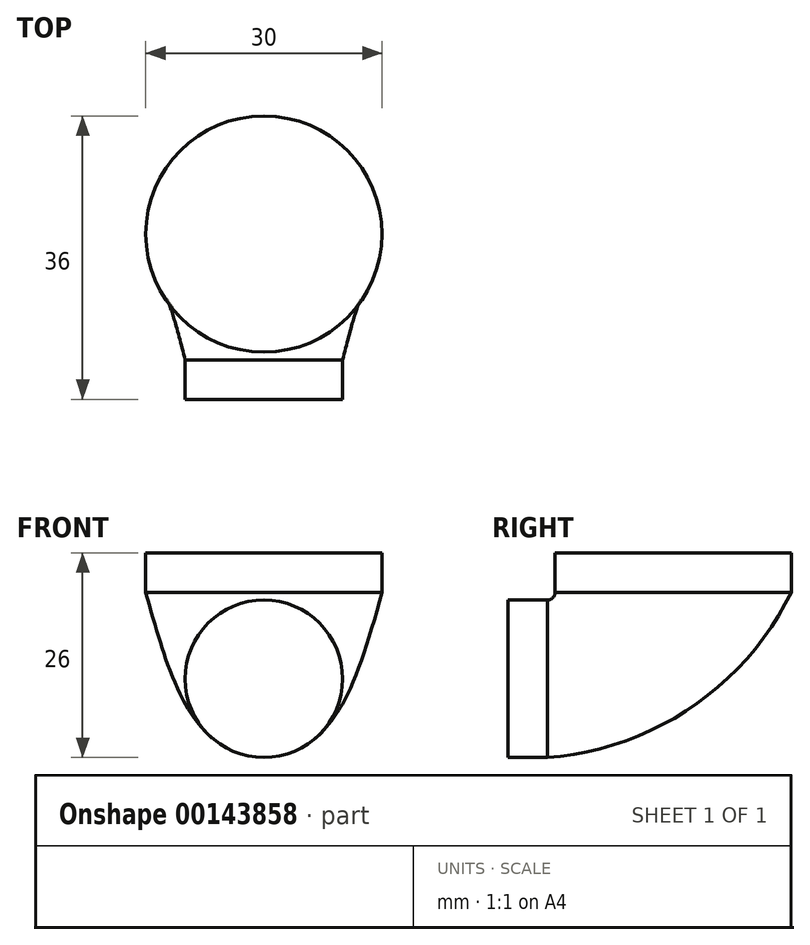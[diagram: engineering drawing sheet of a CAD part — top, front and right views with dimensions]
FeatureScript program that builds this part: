
annotation { "Feature Type Name" : "Feature", "Feature Type Description" : "" }
export const myFeature = defineFeature(function(context is Context, id is Id, definition is map)
    precondition{}
    {
        {
            var Q0;
            Q0=qCreatedBy(makeId("Front.planeOp"),FACE);
            var sketch = newSketch(context, id + "F0", { "sketchPlane" : qUnion([Q0])});
            skArc(sketch, "E0", {"start": v(0, -1) * mm, "mid": v(-10, -11) * mm, "end": v(0, -21) * mm});
            skArc(sketch, "E1", {"start": v(0, -21) * mm, "mid": v(10, -11) * mm, "end": v(0, -1) * mm});
            skSolve(sketch);
        }
        {
            var Q0;
            Q0=qCreatedBy(makeId("Top.planeOp"),FACE);
            var sketch = newSketch(context, id + "F1", { "sketchPlane" : qUnion([Q0])});
            skArc(sketch, "E2", {"start": v(0, 1) * mm, "mid": v(15, 16) * mm, "end": v(0, 31) * mm});
            skArc(sketch, "E3", {"start": v(0, 31) * mm, "mid": v(-15, 16) * mm, "end": v(0, 1) * mm});
            skSolve(sketch);
        }
        {
            var Q0;
            Q0=makeQuery(id+"F0.imprint","IMPRINT",FACE,{"disambiguationData":[TD([[makeQuery(id+"F0.imprint","IMPRINT",EDGE,{"derivedFrom":sQuery(id+"F0.wireOp",EDGE,"E0")}),1.0]])]});
            var Q1;
            Q1=sQuery(id+"F0.wireOp",EDGE,"XV6DxvZN-RSMz-Y8oa-aLI7-YXQPnGix4pax");
            extrude(context, id + "F2", {"entities" : qUnion([Q0]), "surfaceEntities" : qUnion([Q1]), "depth" : 5 * mm});
        }
        {
            var Q0;
            Q0=qSketchRegion(id+"F1",true);
            var Q1;
            Q1=sQuery(id+"F1.wireOp",EDGE,"vkJYqXJf-UWR4-7VrY-OtlE-8EZOiz4KMQL3");
            extrude(context, id + "F3", {"entities" : qUnion([Q0]), "surfaceEntities" : qUnion([Q1]), "depth" : 5 * mm});
        }
        {
            var Q0;
            Q0=qCreatedBy(makeId("Front.planeOp"),FACE);
            cPlane(context, id + "F4", {"entities" : qUnion([Q0]), "cplaneType" : CPlaneType.OFFSET, "offset" : 30 * mm, "oppositeDirection" : true, "width" : 150 * mm, "height" : 150 * mm});
        }
        {
            var Q0;
            Q0=qCreatedBy(makeId("Right.planeOp"),FACE);
            var sketch = newSketch(context, id + "F5", { "sketchPlane" : qUnion([Q0])});
            skArc(sketch, "E4", {"start": v(0, -1) * mm, "mid": v(0.7, -0.7) * mm, "end": v(1, 0) * mm});
            skArc(sketch, "E5", {"start": v(0, -21) * mm, "mid": v(18.3, -14.64) * mm, "end": v(31, 0) * mm});
            skSolve(sketch);
        }
        {
            var Q0;
            Q0=makeQuery(id+"F0.imprint","IMPRINT",FACE,{"disambiguationData":[TD([[makeQuery(id+"F0.imprint","IMPRINT",EDGE,{"derivedFrom":sQuery(id+"F0.wireOp",EDGE,"E0")}),1.0]])]});
            var Q1;
            Q1=makeQuery(id+"F1.imprint","IMPRINT",FACE,{"disambiguationData":[TD([[makeQuery(id+"F1.imprint","IMPRINT",EDGE,{"derivedFrom":sQuery(id+"F1.wireOp",EDGE,"E2")}),1.0]])]});
            var Q2;
            Q2=sQuery(id+"F5.wireOp",EDGE,"E5");
            var Q3;
            Q3=sQuery(id+"F5.wireOp",EDGE,"E4");
            var Q4;
            Q4=sQuery(id+"F5.wireOp",VERTEX,"E5.start");
            var Q5;
            Q5=sQuery(id+"F1.wireOp",VERTEX,"E3.start");
            loft(context, id + "F6", {"operationType" : NewBodyOperationType.ADD, "addGuides" : true, "sheetProfilesArray" : [{ "sheetProfileEntities" : qUnion([Q0]) }, { "sheetProfileEntities" : qUnion([Q1]) }], "guidesArray" : [{ "guideEntities" : qUnion([Q2]), "guideDerivativeType" : LoftGuideDerivativeType.DEFAULT, "guideDerivativeMagnitude" : 1 }, { "guideEntities" : qUnion([Q3]), "guideDerivativeType" : LoftGuideDerivativeType.DEFAULT, "guideDerivativeMagnitude" : 1 }], "matchConnections" : true, "connections" : [{ "connectionEntities" : qUnion([Q4, Q5]), "connectionEdgeQueries" : qUnion([]), "connectionEdgeParameters" : [] }]});
        }
    });
